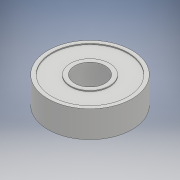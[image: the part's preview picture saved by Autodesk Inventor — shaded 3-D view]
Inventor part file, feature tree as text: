
AUTODESK INVENTOR PART (.ipt)
format: ipt  version: 2017 (Build 210142000, 142)  size: 117,760 bytes
history: native  units: mm
features: extrude x2, sketch x1
ambient origin geometry x8: Origin, YZ Plane, XZ Plane, XY Plane, X Axis, Y Axis, Z Axis, Center Point
bodies: Solid1 (feature_tree)
feature tree (3):
  sketch  "Sketch1"  dims[d0=22.0mm d1=8.0mm d2=7.0mm d3=0.0mm d4=6.5mm d5=0.0mm]
  extrude  "Extrusion1"  Depth=6.5mm
  extrude  "Extrusion2"  Depth=7.0mm TaperAngle=0.0deg
